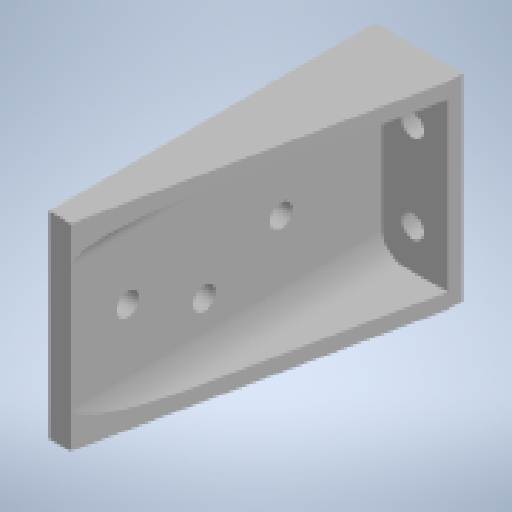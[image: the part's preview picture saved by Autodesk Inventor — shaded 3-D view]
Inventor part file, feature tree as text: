
AUTODESK INVENTOR PART (.ipt)
format: ipt  version: 2023 (Build 270158000, 158)  size: 190,464 bytes
history: native  units: in
note: dims shown in document units (in); Inventor stores cm internally (conversion verified against a paired STEP export)
features: extrude x5, sketch x5, fillet x2
ambient origin geometry x8: Origin, YZ Plane, XZ Plane, XY Plane, X Axis, Y Axis, Z Axis, Center Point
bodies: Solid1 (feature_tree)
feature tree (12):
  extrude  "Extrusion1"  Depth=0.7874in
  extrude  "Extrusion2"  Depth=2.1654in TaperAngle=0.0deg
  extrude  "Extrusion3"  Depth=1.378in
  extrude  "Extrusion4"  Depth=0.5906in
  extrude  "Extrusion5"  Depth=0.1181in TaperAngle=0.0deg
  fillet  "Fillet1"  Radius=0.1378in
  fillet  "Fillet2"  Radius=0.1378in
  sketch  "Sketch1"  dims[d0=2.7953in d1=0.7874in]
  sketch  "Sketch2"  dims[d2=0.1969in d3=2.1654in d4=0.0in]
  sketch  "Sketch3"  dims[d5=0.2008in d6=1.378in]
  sketch  "Sketch5"  dims[d7=0.2992in d8=0.5906in]
  sketch  "Sketch6"  dims[d9=1.2008in d10=1.7717in d11=0.0in d12=0.1378in d13=0.1378in d14=0.1969in d15=0.1969in d16=0.0in d17=0.0in d18=0.1378in d19=0.0in d20=0.2in d21=1.1811in d22=0.315in d23=0.0in d24=0.0in d25=0.1181in d26=0.1181in]
